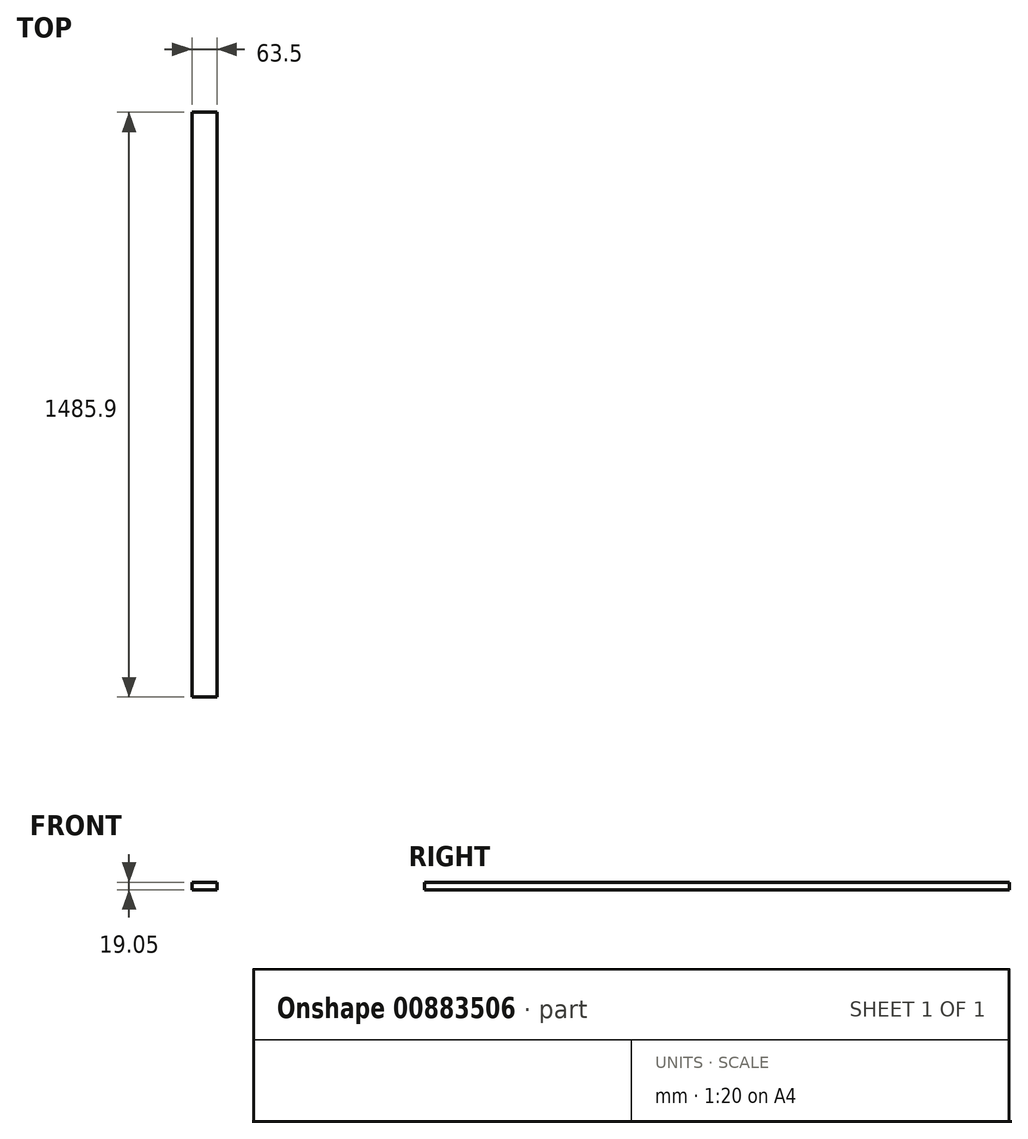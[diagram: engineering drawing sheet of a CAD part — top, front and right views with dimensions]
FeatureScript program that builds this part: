
annotation { "Feature Type Name" : "Feature", "Feature Type Description" : "" }
export const myFeature = defineFeature(function(context is Context, id is Id, definition is map)
    precondition{}
    {
        {
            var Q0;
            Q0=qCreatedBy(makeId("Front.planeOp"),FACE);
            var sketch = newSketch(context, id + "F0", { "sketchPlane" : qUnion([Q0])});
            skLineSegment(sketch, "E0.bottom", {"start": v(0, 0) * mm, "end": v(63.5, 0) * mm});
            skLineSegment(sketch, "E0.top", {"start": v(0, 19.05) * mm, "end": v(63.5, 19.05) * mm});
            skLineSegment(sketch, "E0.left", {"start": v(0, 0) * mm, "end": v(0, 19.05) * mm});
            skLineSegment(sketch, "E0.right", {"start": v(63.5, 0) * mm, "end": v(63.5, 19.05) * mm});
            skSolve(sketch);
        }
        {
            var Q0;
            Q0=qSketchRegion(id+"F0",true);
            extrude(context, id + "F1", {"entities" : qUnion([Q0]), "oppositeDirection" : true, "depth" : 1485.9 * mm, "offsetDistance" : 25.4 * mm});
        }
    });
